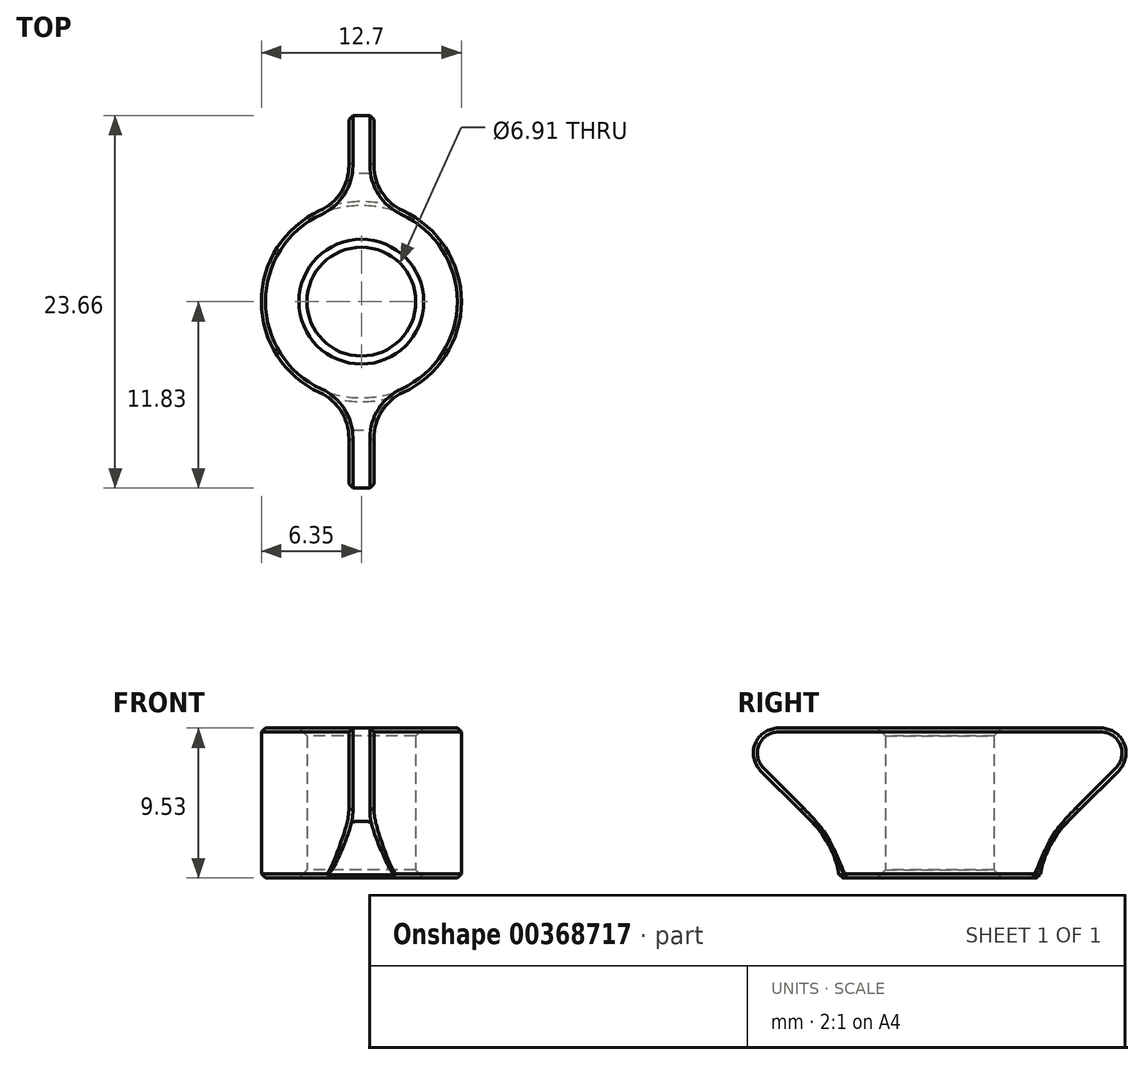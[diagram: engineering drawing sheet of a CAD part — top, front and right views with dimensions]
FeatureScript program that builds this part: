
annotation { "Feature Type Name" : "Feature", "Feature Type Description" : "" }
export const myFeature = defineFeature(function(context is Context, id is Id, definition is map)
    precondition{}
    {
        {
            var Q0;
            Q0=qCreatedBy(makeId("Top.planeOp"),FACE);
            var sketch = newSketch(context, id + "F0", { "sketchPlane" : qUnion([Q0])});
            skCircle(sketch, "E0", {"center": v(0, 0) * mm, "radius": 6.35 * mm});
            skCircle(sketch, "E1", {"center": v(0, 0) * mm, "radius": 3.45 * mm});
            skSolve(sketch);
        }
        {
            var Q0;
            Q0 = qSketchRegion(id + "F0", true);
            extrude(context, id + "F1", {"entities" : qUnion([Q0]), "depth" : 9.52 * mm});
        }
        {
            var Q0;
            Q0=qCreatedBy(makeId("Right.planeOp"),FACE);
            var sketch = newSketch(context, id + "F2", { "sketchPlane" : qUnion([Q0])});
            skLineSegment(sketch, "E2.0", {"start": v(-6.35, 9.53) * mm, "end": v(6.35, 9.53) * mm});
            skLineSegment(sketch, "E3", {"start": v(-6.35, 9.53) * mm, "end": v(-10.25, 9.53) * mm});
            skLineSegment(sketch, "E4", {"start": v(6.35, 9.52) * mm, "end": v(10.25, 9.52) * mm});
            skLineSegment(sketch, "E5", {"start": v(-6.35, 9.53) * mm, "end": v(-4.8, 9.53) * mm});
            skLineSegment(sketch, "E6", {"start": v(-4.8, 9.53) * mm, "end": v(-4.8, 0.26) * mm});
            skLineSegment(sketch, "E7", {"start": v(-4.8, 0) * mm, "end": v(-6.35, 0) * mm});
            skLineSegment(sketch, "E8", {"start": v(6.35, 9.53) * mm, "end": v(4.41, 9.53) * mm});
            skPoint(sketch, "E9.visualSharp", {"position": v(-15.88, 9.53) * mm});
            skLineSegment(sketch, "E9.filletArc", {"start": v(-15.88, 9.53) * mm, "end": v(-15.88, 9.53) * mm});
            skPoint(sketch, "E10.visualSharp", {"position": v(15.87, 9.53) * mm});
            skLineSegment(sketch, "E10.filletArc", {"start": v(15.87, 9.53) * mm, "end": v(15.87, 9.53) * mm});
            skLineSegment(sketch, "E11.0", {"start": v(-11.37, 6.81) * mm, "end": v(-6.81, 2.26) * mm});
            skLineSegment(sketch, "E12.0", {"start": v(11.37, 6.81) * mm, "end": v(6.81, 2.26) * mm});
            skLineSegment(sketch, "E13", {"start": v(5.38, 9.53) * mm, "end": v(5.38, 0.83) * mm});
            skPoint(sketch, "E14.orphan", {"position": v(4.41, 0) * mm});
            skPoint(sketch, "E15.visualSharp", {"position": v(-14.08, 9.53) * mm});
            skArc(sketch, "E15.filletArc", {"start": v(-10.25, 9.53) * mm, "mid": v(-11.71, 8.55) * mm, "end": v(-11.37, 6.81) * mm});
            skPoint(sketch, "E16.visualSharp", {"position": v(14.08, 9.52) * mm});
            skArc(sketch, "E16.filletArc", {"start": v(11.37, 6.81) * mm, "mid": v(11.71, 8.55) * mm, "end": v(10.25, 9.52) * mm});
            skPoint(sketch, "E17.start.orphan", {"position": v(-6.35, 1.8) * mm});
            skLineSegment(sketch, "E18", {"start": v(-6.81, 2.26) * mm, "end": v(-4.8, 0.26) * mm});
            skPoint(sketch, "E19.end.orphan", {"position": v(-6.35, 0) * mm});
            skLineSegment(sketch, "E20", {"start": v(6.81, 2.26) * mm, "end": v(5.38, 0.83) * mm});
            skPoint(sketch, "E21.start.orphan", {"position": v(5.38, 0) * mm});
            skPoint(sketch, "E22.end.orphan", {"position": v(6.35, 0) * mm});
            skSolve(sketch);
        }
        {
            var Q0;
            Q0 = qSketchRegion(id + "F2", true);
            extrude(context, id + "F3", {"entities" : qUnion([Q0]), "operationType" : NewBodyOperationType.ADD, "endBound" : BoundingType.SYMMETRIC, "depth" : 1.59 * mm});
        }
        {
            var Q0;
            Q0=makeQuery(id+"F1.opExtrude","SWEPT_FACE",FACE,{"disambiguationData":[OSD([sQuery(id+"F0.wireOp",EDGE,"E1")])]});
            chamfer(context, id + "F4", {"entities" : qUnion([Q0]), "width" : 0.5 * mm, "tangentPropagation" : true});
        }
        {
            var Q0;
            Q0=makeQuery(id+"F3.boolean.opBoolean","INTERSECT",EDGE,{"derivedFrom":[makeQuery(id+"F1.opExtrude","SWEPT_FACE",FACE,{"disambiguationData":[OSD([sQuery(id+"F0.wireOp",EDGE,"E0")])]}),makeQuery(id+"F3.opExtrude","CAP_FACE",FACE,{"disambiguationData":[OSD([sQuery(id+"F2.wireOp",EDGE,"E4"),sQuery(id+"F2.wireOp",EDGE,"E8"),sQuery(id+"F2.wireOp",EDGE,"E12.0"),sQuery(id+"F2.wireOp",EDGE,"E13"),sQuery(id+"F2.wireOp",EDGE,"E16.filletArc"),sQuery(id+"F2.wireOp",EDGE,"E20")])],"isStart":true})]});
            var Q1;
            Q1=makeQuery(id+"F3.boolean.opBoolean","INTERSECT",EDGE,{"derivedFrom":[makeQuery(id+"F1.opExtrude","SWEPT_FACE",FACE,{"disambiguationData":[OSD([sQuery(id+"F0.wireOp",EDGE,"E0")])]}),makeQuery(id+"F3.opExtrude","CAP_FACE",FACE,{"disambiguationData":[OSD([sQuery(id+"F2.wireOp",EDGE,"E4"),sQuery(id+"F2.wireOp",EDGE,"E8"),sQuery(id+"F2.wireOp",EDGE,"E12.0"),sQuery(id+"F2.wireOp",EDGE,"E13"),sQuery(id+"F2.wireOp",EDGE,"E16.filletArc"),sQuery(id+"F2.wireOp",EDGE,"E20")])],"isStart":false})]});
            var Q2;
            Q2=makeQuery(id+"F3.boolean.opBoolean","INTERSECT",EDGE,{"derivedFrom":[makeQuery(id+"F1.opExtrude","SWEPT_FACE",FACE,{"disambiguationData":[OSD([sQuery(id+"F0.wireOp",EDGE,"E0")])]}),makeQuery(id+"F3.opExtrude","CAP_FACE",FACE,{"disambiguationData":[OSD([sQuery(id+"F2.wireOp",EDGE,"E3"),sQuery(id+"F2.wireOp",EDGE,"E5"),sQuery(id+"F2.wireOp",EDGE,"E6"),sQuery(id+"F2.wireOp",EDGE,"E11.0"),sQuery(id+"F2.wireOp",EDGE,"E15.filletArc"),sQuery(id+"F2.wireOp",EDGE,"E18")])],"isStart":false})]});
            var Q3;
            Q3=makeQuery(id+"F3.boolean.opBoolean","INTERSECT",EDGE,{"derivedFrom":[makeQuery(id+"F1.opExtrude","SWEPT_FACE",FACE,{"disambiguationData":[OSD([sQuery(id+"F0.wireOp",EDGE,"E0")])]}),makeQuery(id+"F3.opExtrude","CAP_FACE",FACE,{"disambiguationData":[OSD([sQuery(id+"F2.wireOp",EDGE,"E3"),sQuery(id+"F2.wireOp",EDGE,"E5"),sQuery(id+"F2.wireOp",EDGE,"E6"),sQuery(id+"F2.wireOp",EDGE,"E11.0"),sQuery(id+"F2.wireOp",EDGE,"E15.filletArc"),sQuery(id+"F2.wireOp",EDGE,"E18")])],"isStart":true})]});
            fillet(context, id + "F5", {"entities" : qUnion([Q0, Q1, Q2, Q3]), "radius" : 3.17 * mm, "tangentPropagation" : true, "allowEdgeOverflow" : false});
        }
        {
            var Q0;
            Q0=makeQuery(id+"F3.boolean.opBoolean","INTERSECT",EDGE,{"derivedFrom":[makeQuery(id+"F1.opExtrude","SWEPT_FACE",FACE,{"disambiguationData":[OSD([sQuery(id+"F0.wireOp",EDGE,"E0")])]}),makeQuery(id+"F3.opExtrude","SWEPT_FACE",FACE,{"disambiguationData":[OSD([sQuery(id+"F2.wireOp",EDGE,"E11.0"),sQuery(id+"F2.wireOp",EDGE,"E18")])]})]});
            var Q1;
            Q1=makeQuery(id+"F3.boolean.opBoolean","INTERSECT",EDGE,{"derivedFrom":[makeQuery(id+"F1.opExtrude","SWEPT_FACE",FACE,{"disambiguationData":[OSD([sQuery(id+"F0.wireOp",EDGE,"E0")])]}),makeQuery(id+"F3.opExtrude","SWEPT_FACE",FACE,{"disambiguationData":[OSD([sQuery(id+"F2.wireOp",EDGE,"E12.0"),sQuery(id+"F2.wireOp",EDGE,"E20")])]})]});
            fillet(context, id + "F6", {"entities" : qUnion([Q0, Q1]), "radius" : 6.35 * mm, "tangentPropagation" : true, "allowEdgeOverflow" : false});
        }
        {
            var Q0;
            Q0=makeQuery(id+"F3.opExtrude","CAP_EDGE",EDGE,{"disambiguationData":[OSD([sQuery(id+"F2.wireOp",EDGE,"E16.filletArc")])],"isStart":true});
            var Q1;
            Q1=makeQuery(id+"F3.opExtrude","CAP_EDGE",EDGE,{"disambiguationData":[OSD([sQuery(id+"F2.wireOp",EDGE,"E16.filletArc")])],"isStart":false});
            var Q2;
            Q2=makeQuery(id+"F1.opExtrude","CAP_EDGE",EDGE,{"disambiguationData":[OSD([sQuery(id+"F0.wireOp",EDGE,"E0")])],"isStart":true});
            chamfer(context, id + "F7", {"entities" : qUnion([Q0, Q1, Q2]), "width" : 0.25 * mm, "tangentPropagation" : true});
        }
        {
            var Q0;
            {var subQ0=sQuery(id+"F0.wireOp",EDGE,"E0");Q0=makeQuery(id+"F6.opFillet","BLEND_EDGE",EDGE,{"blendedFrom":[makeQuery(id+"F3.boolean.opBoolean","INTERSECT",EDGE,{"derivedFrom":[makeQuery(id+"F1.opExtrude","SWEPT_FACE",FACE,{"disambiguationData":[OSD([subQ0])]}),makeQuery(id+"F3.opExtrude","SWEPT_FACE",FACE,{"disambiguationData":[OSD([sQuery(id+"F2.wireOp",EDGE,"E12.0"),sQuery(id+"F2.wireOp",EDGE,"E20")])]})]}),makeQuery(id+"F1.opExtrude","CAP_FACE",FACE,{"disambiguationData":[OSD([subQ0,sQuery(id+"F0.wireOp",EDGE,"E1")])],"isStart":true})],"blendedInto":[makeQuery(id+"F1.opExtrude","CAP_FACE",FACE,{"disambiguationData":[OSD([subQ0,sQuery(id+"F0.wireOp",EDGE,"E1")])],"isStart":true})]});}
            var Q1;
            {var subQ0=sQuery(id+"F0.wireOp",EDGE,"E0");Q1=makeQuery(id+"F6.opFillet","BLEND_EDGE",EDGE,{"blendedFrom":[makeQuery(id+"F3.boolean.opBoolean","INTERSECT",EDGE,{"derivedFrom":[makeQuery(id+"F1.opExtrude","SWEPT_FACE",FACE,{"disambiguationData":[OSD([subQ0])]}),makeQuery(id+"F3.opExtrude","SWEPT_FACE",FACE,{"disambiguationData":[OSD([sQuery(id+"F2.wireOp",EDGE,"E11.0"),sQuery(id+"F2.wireOp",EDGE,"E18")])]})]}),makeQuery(id+"F1.opExtrude","CAP_FACE",FACE,{"disambiguationData":[OSD([subQ0,sQuery(id+"F0.wireOp",EDGE,"E1")])],"isStart":true})],"blendedInto":[makeQuery(id+"F1.opExtrude","CAP_FACE",FACE,{"disambiguationData":[OSD([subQ0,sQuery(id+"F0.wireOp",EDGE,"E1")])],"isStart":true})]});}
            chamfer(context, id + "F8", {"entities" : qUnion([Q0, Q1]), "width" : 0.25 * mm, "tangentPropagation" : true});
        }
    });
